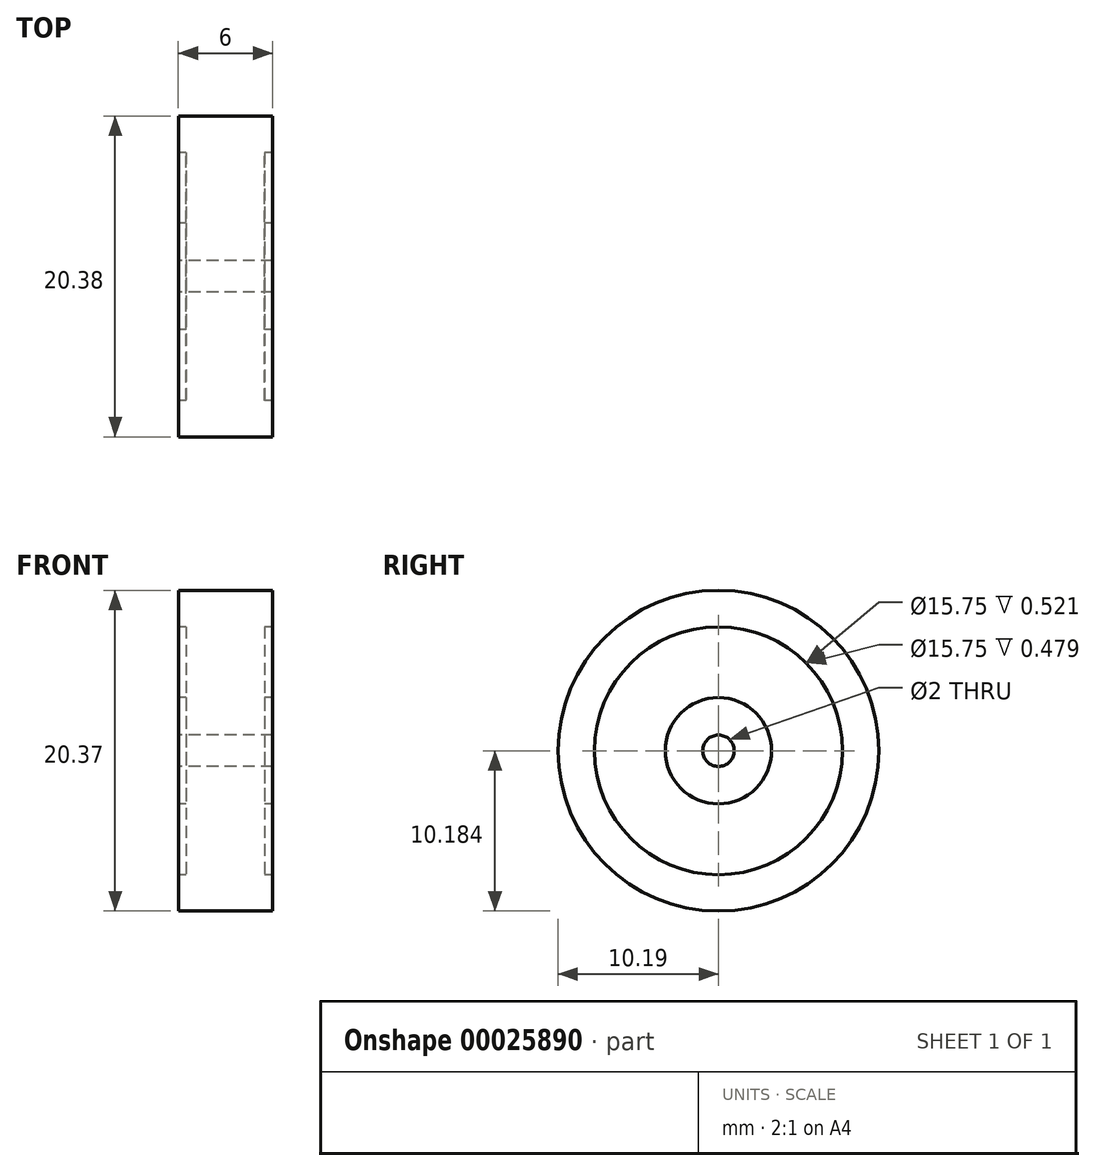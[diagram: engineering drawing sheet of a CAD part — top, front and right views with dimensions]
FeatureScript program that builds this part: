
annotation { "Feature Type Name" : "Feature", "Feature Type Description" : "" }
export const myFeature = defineFeature(function(context is Context, id is Id, definition is map)
    precondition{}
    {
        {
            var Q0;
            Q0=qCreatedBy(makeId("Front.planeOp"),FACE);
            var sketch = newSketch(context, id + "F0", { "sketchPlane" : qUnion([Q0])});
            skLineSegment(sketch, "E0", {"start": v(-55.1, -3.8) * mm, "end": v(-38.6, -3.8) * mm, "construction": true});
            skLineSegment(sketch, "E1.bottom", {"start": v(-50.72, -0.42) * mm, "end": v(-44.72, -0.42) * mm});
            skLineSegment(sketch, "E1.top", {"start": v(-50.72, -2.8) * mm, "end": v(-44.72, -2.8) * mm});
            skLineSegment(sketch, "E1.left", {"start": v(-50.72, -0.42) * mm, "end": v(-50.72, -2.8) * mm});
            skLineSegment(sketch, "E1.right", {"start": v(-44.72, -0.42) * mm, "end": v(-44.72, -2.8) * mm});
            skLineSegment(sketch, "E2.bottom", {"start": v(-50.24, -0.42) * mm, "end": v(-45.24, -0.42) * mm});
            skLineSegment(sketch, "E2.top", {"start": v(-50.24, 4.08) * mm, "end": v(-45.24, 4.08) * mm});
            skLineSegment(sketch, "E2.left", {"start": v(-50.24, -0.42) * mm, "end": v(-50.24, 4.08) * mm});
            skLineSegment(sketch, "E2.right", {"start": v(-45.24, -0.42) * mm, "end": v(-45.24, 4.08) * mm});
            skLineSegment(sketch, "E3.bottom", {"start": v(-50.72, 4.08) * mm, "end": v(-44.72, 4.08) * mm});
            skLineSegment(sketch, "E3.top", {"start": v(-50.72, 6.4) * mm, "end": v(-44.72, 6.4) * mm});
            skLineSegment(sketch, "E3.left", {"start": v(-50.72, 4.08) * mm, "end": v(-50.72, 6.4) * mm});
            skLineSegment(sketch, "E3.right", {"start": v(-44.72, 4.08) * mm, "end": v(-44.72, 6.4) * mm});
            skSolve(sketch);
        }
        {
            var Q0;
            Q0 = qSketchRegion(id + "F0", true);
            var Q1;
            Q1=sQuery(id+"F0.wireOp",EDGE,"E0");
            revolve(context, id + "F1", {"entities" : qUnion([Q0]), "axis" : qUnion([Q1]), "revolveType" : RevolveType.FULL});
        }
    });
